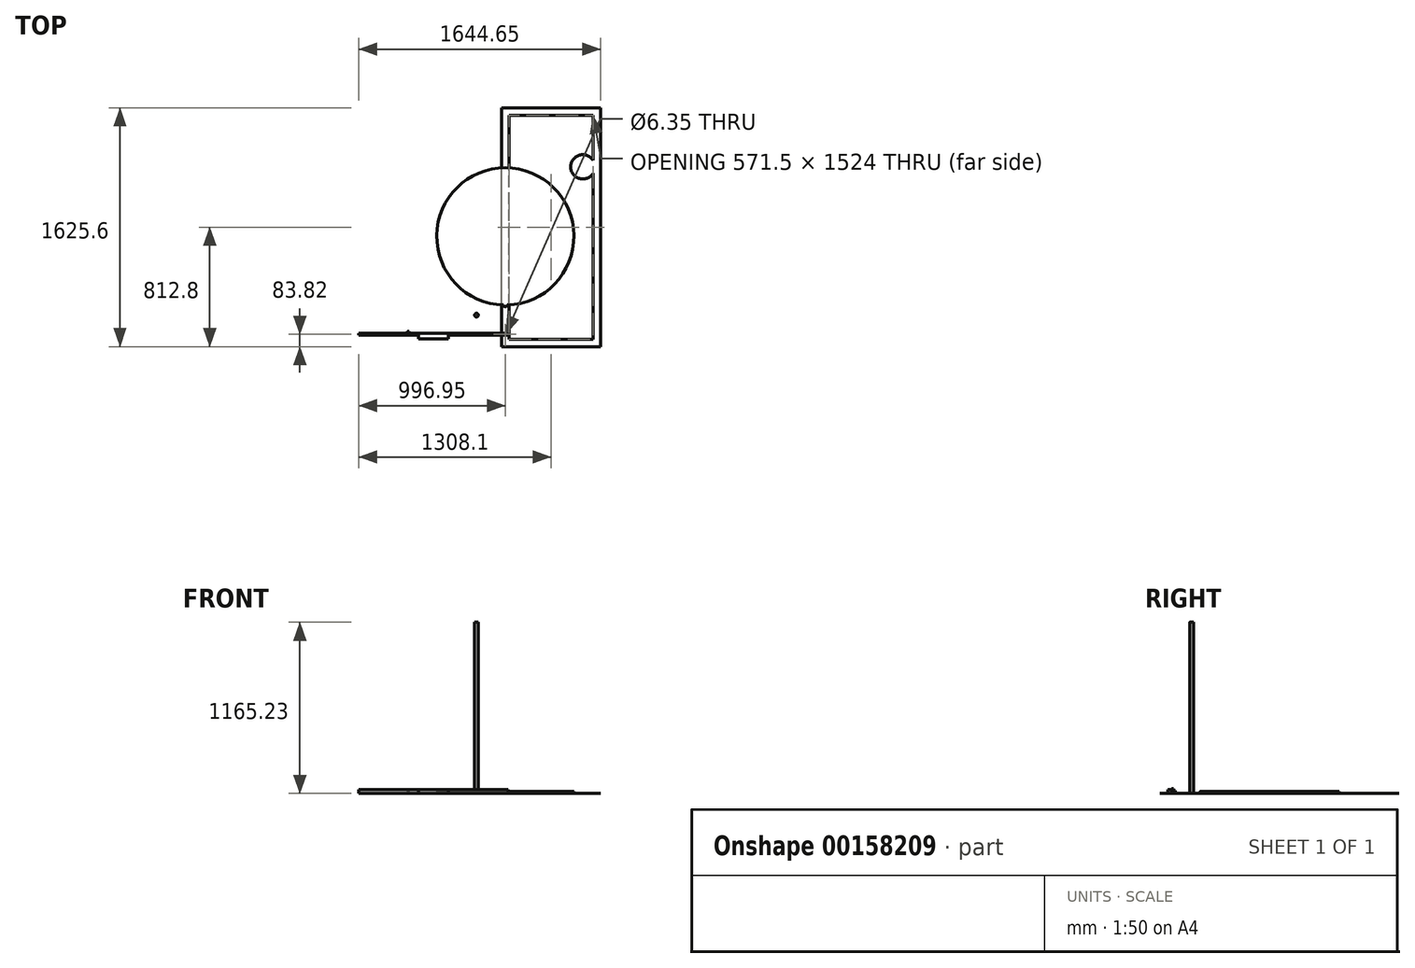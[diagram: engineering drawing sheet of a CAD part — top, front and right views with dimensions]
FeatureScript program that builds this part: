
annotation { "Feature Type Name" : "Feature", "Feature Type Description" : "" }
export const myFeature = defineFeature(function(context is Context, id is Id, definition is map)
    precondition{}
    {
        {
            var Q0;
            Q0=qCreatedBy(makeId("Top.planeOp"),FACE);
            var sketch = newSketch(context, id + "F0", { "sketchPlane" : qUnion([Q0])});
            skLineSegment(sketch, "E0.bottom", {"start": v(19.05, -6.35) * mm, "end": v(-996.95, -6.35) * mm});
            skLineSegment(sketch, "E0.top", {"start": v(19.05, 6.35) * mm, "end": v(-996.95, 6.35) * mm});
            skLineSegment(sketch, "E0.left", {"start": v(19.05, -6.35) * mm, "end": v(19.05, 6.35) * mm});
            skLineSegment(sketch, "E0.right", {"start": v(-996.95, -6.35) * mm, "end": v(-996.95, 6.35) * mm});
            skLineSegment(sketch, "E1", {"start": v(-996.95, 0) * mm, "end": v(19.05, 0) * mm, "construction": true});
            skCircle(sketch, "E2", {"center": v(0, 0) * mm, "radius": 3.18 * mm});
            skSolve(sketch);
        }
        {
            var Q0;
            Q0=makeQuery(id+"F0.imprint","IMPRINT",FACE,{"disambiguationData":[TD([[makeQuery(id+"F0.imprint","IMPRINT",EDGE,{"derivedFrom":sQuery(id+"F0.wireOp",EDGE,"E0.bottom")}),-1.0]])]});
            extrude(context, id + "F1", {"entities" : qUnion([Q0]), "depth" : 25.4 * mm});
        }
        {
            var Q0;
            Q0=makeQuery(id+"F1.opExtrude","SWEPT_FACE",FACE,{"disambiguationData":[OSD([sQuery(id+"F0.wireOp",EDGE,"E0.top")])]});
            var sketch = newSketch(context, id + "F2", { "sketchPlane" : qUnion([Q0])});
            skCircle(sketch, "E3", {"center": v(660.4, 12.7) * mm, "radius": 6.35 * mm});
            skPoint(sketch, "E3.centerSnap0", {"position": v(996.95, 12.7) * mm});
            skSolve(sketch);
        }
        {
            var Q0;
            Q0=makeQuery(id+"F2.imprint","IMPRINT",FACE,{"disambiguationData":[TD([[makeQuery(id+"F2.imprint","IMPRINT",EDGE,{"derivedFrom":sQuery(id+"F2.wireOp",EDGE,"E3")}),1.0]])]});
            extrude(context, id + "F3", {"entities" : qUnion([Q0]), "operationType" : NewBodyOperationType.ADD, "depth" : 12.7 * mm});
        }
        {
            var Q0;
            Q0=qCreatedBy(makeId("Top.planeOp"),FACE);
            var sketch = newSketch(context, id + "F4", { "sketchPlane" : qUnion([Q0])});
            skArc(sketch, "E4", {"start": v(12.7, 199.78) * mm, "mid": v(0, 1133.06) * mm, "end": v(-12.7, 199.78) * mm});
            skArc(sketch, "E5", {"start": v(-12.7, 199.78) * mm, "mid": v(0, 186.91) * mm, "end": v(12.7, 199.78) * mm});
            skSolve(sketch);
        }
        {
            var Q0;
            Q0=makeQuery(id+"F4.imprint","IMPRINT",FACE,{"disambiguationData":[TD([[makeQuery(id+"F4.imprint","IMPRINT",EDGE,{"derivedFrom":sQuery(id+"F4.wireOp",EDGE,"E4")}),1.0]])]});
            extrude(context, id + "F5", {"entities" : qUnion([Q0]), "depth" : 12.7 * mm});
        }
        {
            var Q0;
            Q0=qCreatedBy(makeId("Top.planeOp"),FACE);
            var sketch = newSketch(context, id + "F6", { "sketchPlane" : qUnion([Q0])});
            skCircle(sketch, "E6", {"center": v(-195.98, 130.7) * mm, "radius": 12.7 * mm});
            skSolve(sketch);
        }
        {
            var Q0;
            Q0=makeQuery(id+"F6.imprint","IMPRINT",FACE,{"disambiguationData":[TD([[makeQuery(id+"F6.imprint","IMPRINT",EDGE,{"derivedFrom":sQuery(id+"F6.wireOp",EDGE,"E6")}),1.0]])]});
            extrude(context, id + "F7", {"entities" : qUnion([Q0]), "depth" : 1165.22 * mm});
        }
        {
            var Q0;
            Q0=makeQuery(id+"F1.opExtrude","SWEPT_FACE",FACE,{"disambiguationData":[OSD([sQuery(id+"F0.wireOp",EDGE,"E0.bottom")])]});
            var sketch = newSketch(context, id + "F8", { "sketchPlane" : qUnion([Q0])});
            skArc(sketch, "E7", {"start": v(-666.75, 25.4) * mm, "mid": v(-662.26, 27.26) * mm, "end": v(-660.4, 31.75) * mm});
            skArc(sketch, "E8", {"start": v(-660.4, 31.75) * mm, "mid": v(-658.54, 27.26) * mm, "end": v(-654.05, 25.4) * mm});
            skLineSegment(sketch, "E9", {"start": v(-666.75, 25.4) * mm, "end": v(-654.05, 25.4) * mm});
            skSolve(sketch);
        }
        {
            var Q0;
            Q0=makeQuery(id+"F8.imprint","IMPRINT",FACE,{"disambiguationData":[TD([[makeQuery(id+"F8.imprint","IMPRINT",EDGE,{"derivedFrom":sQuery(id+"F8.wireOp",EDGE,"E7")}),-1.0]])]});
            extrude(context, id + "F9", {"entities" : qUnion([Q0]), "operationType" : NewBodyOperationType.ADD, "oppositeDirection" : true, "depth" : 12.7 * mm});
        }
        {
            var Q0;
            Q0=makeQuery(id+"F9.boolean.opBoolean","MERGE",FACE,{"derivedFrom":[makeQuery(id+"F1.opExtrude","SWEPT_FACE",FACE,{"disambiguationData":[OSD([sQuery(id+"F0.wireOp",EDGE,"E0.bottom")])]}),makeQuery(id+"F9.opExtrude","CAP_FACE",FACE,{"disambiguationData":[OSD([sQuery(id+"F8.wireOp",EDGE,"E7"),sQuery(id+"F8.wireOp",EDGE,"E8"),sQuery(id+"F8.wireOp",EDGE,"E9")])],"isStart":true})]});
            var sketch = newSketch(context, id + "F10", { "sketchPlane" : qUnion([Q0])});
            skLineSegment(sketch, "E10.bottom", {"start": v(-387.35, 25.4) * mm, "end": v(-590.55, 25.4) * mm});
            skLineSegment(sketch, "E10.top", {"start": v(-387.35, 0) * mm, "end": v(-590.55, 0) * mm});
            skLineSegment(sketch, "E10.left", {"start": v(-387.35, 25.4) * mm, "end": v(-387.35, 0) * mm});
            skLineSegment(sketch, "E10.right", {"start": v(-590.55, 25.4) * mm, "end": v(-590.55, 0) * mm});
            skPoint(sketch, "E10.middle", {"position": v(-488.95, 12.7) * mm});
            skPoint(sketch, "E10.middle.positionSnap0", {"position": v(-488.95, 0) * mm});
            skPoint(sketch, "E10.middle.positionSnap1", {"position": v(-996.95, 12.7) * mm});
            skPoint(sketch, "E10.centerSnap0", {"position": v(-488.95, 0) * mm});
            skPoint(sketch, "E10.centerSnap1", {"position": v(-996.95, 12.7) * mm});
            skSolve(sketch);
        }
        {
            var Q0;
            Q0=makeQuery(id+"F10.imprint","IMPRINT",FACE,{"disambiguationData":[TD([[makeQuery(id+"F10.imprint","IMPRINT",EDGE,{"derivedFrom":sQuery(id+"F10.wireOp",EDGE,"E10.bottom")}),1.0]])]});
            extrude(context, id + "F11", {"entities" : qUnion([Q0]), "operationType" : NewBodyOperationType.ADD, "depth" : 25.4 * mm});
        }
        {
            var Q0;
            Q0=qCreatedBy(makeId("Top.planeOp"),FACE);
            var sketch = newSketch(context, id + "F12", { "sketchPlane" : qUnion([Q0])});
            skLineSegment(sketch, "E11.bottom", {"start": v(25.4, -83.82) * mm, "end": v(-25.4, -83.82) * mm});
            skLineSegment(sketch, "E11.top", {"start": v(25.4, 1541.78) * mm, "end": v(-25.4, 1541.78) * mm});
            skLineSegment(sketch, "E11.left", {"start": v(25.4, -83.82) * mm, "end": v(25.4, 1541.78) * mm});
            skLineSegment(sketch, "E11.right", {"start": v(-25.4, -83.82) * mm, "end": v(-25.4, 1541.78) * mm});
            skPoint(sketch, "E11.middle", {"position": v(0, 728.98) * mm});
            skLineSegment(sketch, "E12.bottom", {"start": v(25.4, 1541.78) * mm, "end": v(596.9, 1541.78) * mm});
            skLineSegment(sketch, "E12.top", {"start": v(25.4, 1490.98) * mm, "end": v(596.9, 1490.98) * mm});
            skLineSegment(sketch, "E12.left", {"start": v(25.4, 1541.78) * mm, "end": v(25.4, 1490.98) * mm});
            skLineSegment(sketch, "E12.right", {"start": v(596.9, 1541.78) * mm, "end": v(596.9, 1490.98) * mm});
            skLineSegment(sketch, "E13.bottom", {"start": v(25.4, -83.82) * mm, "end": v(596.9, -83.82) * mm});
            skLineSegment(sketch, "E13.top", {"start": v(25.4, -33.02) * mm, "end": v(596.9, -33.02) * mm});
            skLineSegment(sketch, "E13.left", {"start": v(25.4, -83.82) * mm, "end": v(25.4, -33.02) * mm});
            skLineSegment(sketch, "E13.right", {"start": v(596.9, -83.82) * mm, "end": v(596.9, -33.02) * mm});
            skLineSegment(sketch, "E14.bottom", {"start": v(596.9, -83.82) * mm, "end": v(647.7, -83.82) * mm});
            skLineSegment(sketch, "E14.top", {"start": v(596.9, 1541.78) * mm, "end": v(647.7, 1541.78) * mm});
            skLineSegment(sketch, "E14.left", {"start": v(596.9, -83.82) * mm, "end": v(596.9, 1541.78) * mm});
            skLineSegment(sketch, "E14.right", {"start": v(647.7, -83.82) * mm, "end": v(647.7, 1541.78) * mm});
            skCircle(sketch, "E15", {"center": v(527.05, 1139.83) * mm, "radius": 82.55 * mm});
            skSolve(sketch);
        }
        {
            var Q0;
            Q0=makeQuery(id+"F12.imprint","IMPRINT",FACE,{"disambiguationData":[TD([[makeQuery(id+"F12.imprint","IMPRINT",EDGE,{"derivedFrom":sQuery(id+"F12.wireOp",EDGE,"E11.bottom")}),-1.0]])]});
            var Q1;
            {var subQ0=sQuery(id+"F12.wireOp",EDGE,"E12.bottom");Q1=makeQuery(id+"F12.imprint","IMPRINT",FACE,{"disambiguationData":[TD([[makeQuery(id+"F12.imprint","IMPRINT",EDGE,{"derivedFrom":subQ0}),-1.0]])]});}
            var Q2;
            {var subQ6=sQuery(id+"F12.wireOp",EDGE,"E14.bottom");Q2=makeQuery(id+"F12.imprint","IMPRINT",FACE,{"disambiguationData":[TD([[makeQuery(id+"F12.imprint","IMPRINT",EDGE,{"derivedFrom":subQ6}),1.0]])]});}
            var Q3;
            {var subQ0=sQuery(id+"F12.wireOp",EDGE,"E15");var subQ1=sQuery(id+"F12.wireOp",EDGE,"E14.left");var subQ2=makeQuery(id+"F12.imprint","INTERSECT",VERTEX,{"disambiguationData":[OD(0.0)],"derivedFrom":[subQ1,subQ0]});Q3=makeQuery(id+"F12.imprint","IMPRINT",FACE,{"disambiguationData":[TD([[makeQuery(id+"F12.imprint","IMPRINT",EDGE,{"disambiguationData":[TD([[subQ2,-1.0]])],"derivedFrom":subQ1}),1.0]])]});}
            var Q4;
            {var subQ0=sQuery(id+"F12.wireOp",EDGE,"E15");var subQ1=sQuery(id+"F12.wireOp",EDGE,"E14.left");var subQ2=makeQuery(id+"F12.imprint","INTERSECT",VERTEX,{"disambiguationData":[OD(0.0)],"derivedFrom":[subQ1,subQ0]});Q4=makeQuery(id+"F12.imprint","IMPRINT",FACE,{"disambiguationData":[TD([[makeQuery(id+"F12.imprint","IMPRINT",EDGE,{"disambiguationData":[TD([[subQ2,-1.0]])],"derivedFrom":subQ1}),-1.0]])]});}
            var Q5;
            {var subQ0=sQuery(id+"F12.wireOp",EDGE,"E13.bottom");Q5=makeQuery(id+"F12.imprint","IMPRINT",FACE,{"disambiguationData":[TD([[makeQuery(id+"F12.imprint","IMPRINT",EDGE,{"derivedFrom":subQ0}),1.0]])]});}
            extrude(context, id + "F13", {"entities" : qUnion([Q0, Q1, Q2, Q3, Q4, Q5]), "depth" : 2.54 * mm});
        }
    });
